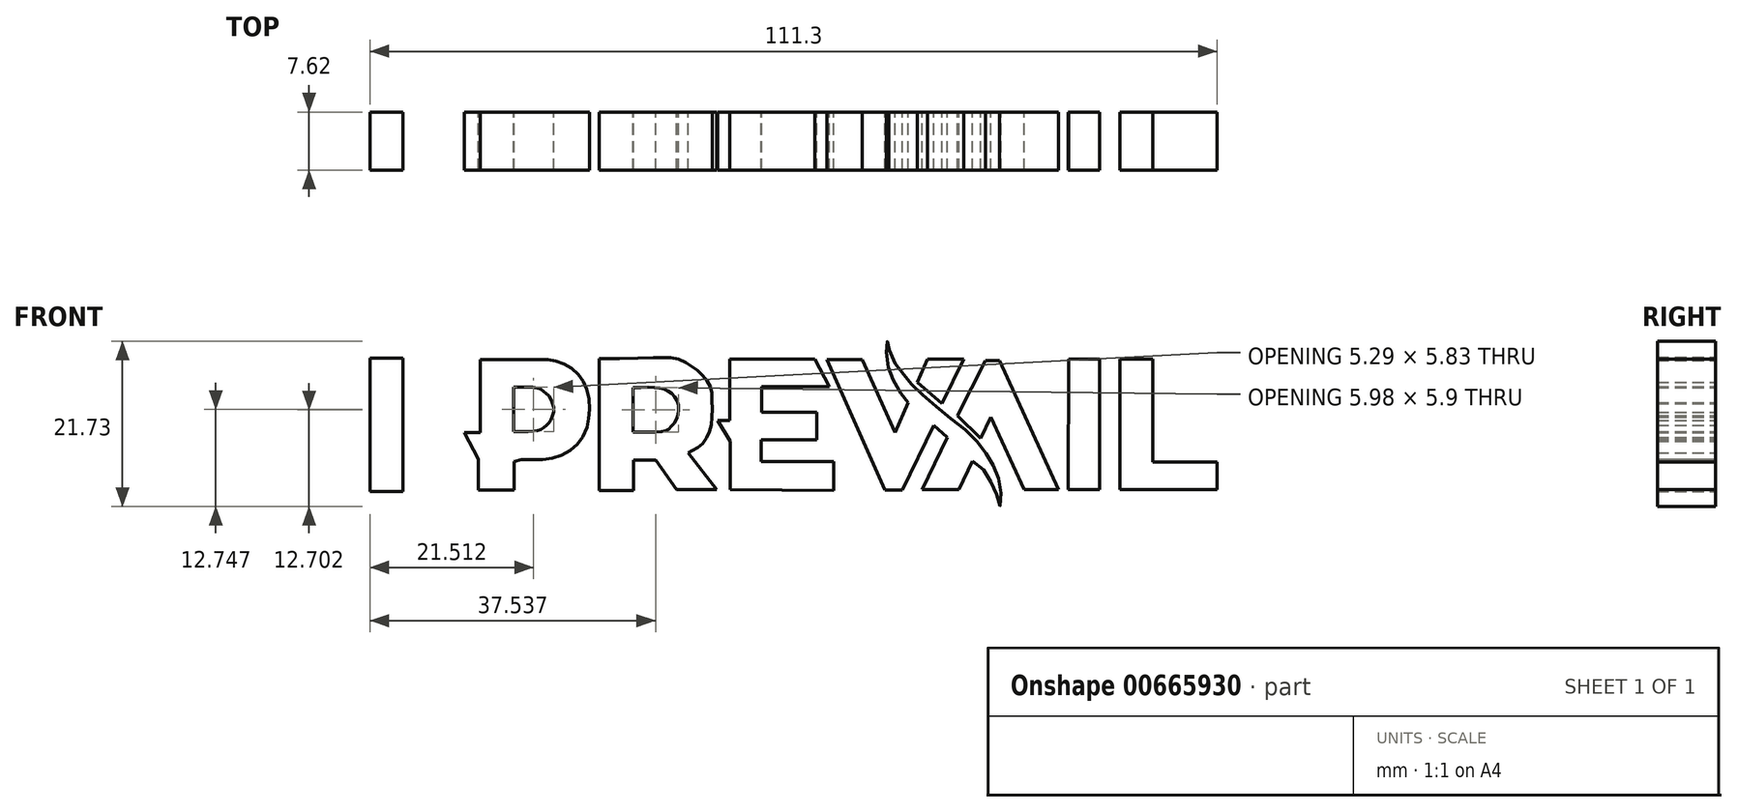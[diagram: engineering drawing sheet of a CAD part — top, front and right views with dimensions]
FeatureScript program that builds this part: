
annotation { "Feature Type Name" : "Feature", "Feature Type Description" : "" }
export const myFeature = defineFeature(function(context is Context, id is Id, definition is map)
    precondition{}
    {
        {
            var Q0;
            Q0=qCreatedBy(makeId("Front.planeOp"),FACE);
            var sketch = newSketch(context, id + "F0", { "sketchPlane" : qUnion([Q0])});
            skLineSegment(sketch, "E0", {"start": v(-55.42, 8.61) * mm, "end": v(-51.05, 8.61) * mm});
            skLineSegment(sketch, "E1", {"start": v(-51.05, 8.61) * mm, "end": v(-51.05, -8.88) * mm});
            skLineSegment(sketch, "E2", {"start": v(-51.05, -8.88) * mm, "end": v(-55.4, -8.88) * mm});
            skLineSegment(sketch, "E3", {"start": v(-55.4, -8.88) * mm, "end": v(-55.42, 8.61) * mm});
            skLineSegment(sketch, "E4", {"start": v(-43, -1.15) * mm, "end": v(-40.93, -1.15) * mm});
            skLineSegment(sketch, "E5", {"start": v(-40.93, -1.15) * mm, "end": v(-40.93, 8.45) * mm});
            skLineSegment(sketch, "E6", {"start": v(-43, -1.15) * mm, "end": v(-41.17, -4.64) * mm});
            skLineSegment(sketch, "E7", {"start": v(-41.17, -4.64) * mm, "end": v(-41.17, -8.71) * mm});
            skLineSegment(sketch, "E8", {"start": v(-41.17, -8.71) * mm, "end": v(-36.49, -8.71) * mm});
            skLineSegment(sketch, "E9", {"start": v(-36.49, -8.71) * mm, "end": v(-36.49, -4.95) * mm});
            skLineSegment(sketch, "E10", {"start": v(-36.55, 4.78) * mm, "end": v(-36.55, -1.05) * mm});
            skFitSpline(sketch, "E11", {"points": [v(-40.93, 8.45) * mm, v(-33.7, 8.45) * mm, v(-32.38, 8.45) * mm, v(-31.47, 8.34) * mm, v(-30.55, 8.07) * mm, v(-29.4, 7.62) * mm, v(-28.36, 6.8) * mm, v(-27.68, 6) * mm, v(-27.12, 5) * mm, v(-26.72, 3.78) * mm, v(-26.55, 2.03) * mm, v(-26.68, 0.64) * mm, v(-26.87, -0.46) * mm, v(-27.62, -2.02) * mm, v(-28.35, -2.86) * mm, v(-29.63, -3.85) * mm, v(-30.87, -4.4) * mm, v(-32.43, -4.68) * mm, v(-33.8, -4.69) * mm, v(-35.75, -4.72) * mm, v(-36.49, -4.95) * mm], "startDerivative": vector(78.04, -0.5) * mm, "endDerivative": vector(-6.77, -22.55) * mm});
            skFitSpline(sketch, "E12", {"points": [v(-36.55, 4.78) * mm, v(-34.11, 4.78) * mm, v(-33.12, 4.59) * mm, v(-32.49, 4.14) * mm, v(-31.95, 3.67) * mm, v(-31.5, 2.82) * mm, v(-31.26, 1.8) * mm, v(-31.59, 0.62) * mm, v(-31.99, 0) * mm, v(-32.59, -0.49) * mm, v(-33.17, -0.85) * mm, v(-33.87, -0.97) * mm, v(-36.55, -1.05) * mm], "startDerivative": vector(21.47, 0.42) * mm, "endDerivative": vector(-23.73, -0.4) * mm});
            skLineSegment(sketch, "E13", {"start": v(-25.3, -8.76) * mm, "end": v(-20.82, -8.76) * mm});
            skLineSegment(sketch, "E14", {"start": v(-20.82, -8.76) * mm, "end": v(-20.82, -4.8) * mm});
            skLineSegment(sketch, "E15", {"start": v(-20.82, -4.8) * mm, "end": v(-17.85, -4.8) * mm});
            skLineSegment(sketch, "E16", {"start": v(-17.85, -4.8) * mm, "end": v(-15.14, -8.67) * mm});
            skLineSegment(sketch, "E17", {"start": v(-15.14, -8.67) * mm, "end": v(-9.87, -8.67) * mm});
            skLineSegment(sketch, "E18", {"start": v(-9.87, -8.67) * mm, "end": v(-13.63, -3.85) * mm});
            skLineSegment(sketch, "E19", {"start": v(-25.3, -8.76) * mm, "end": v(-25.3, 8.55) * mm});
            skLineSegment(sketch, "E20", {"start": v(-20.87, -1.13) * mm, "end": v(-20.87, 4.72) * mm});
            skLineSegment(sketch, "E21", {"start": v(-8.12, -8.66) * mm, "end": v(-8.12, -2.32) * mm});
            skLineSegment(sketch, "E22", {"start": v(-8.12, -2.32) * mm, "end": v(-9.76, 0.46) * mm});
            skLineSegment(sketch, "E23", {"start": v(-9.76, 0.46) * mm, "end": v(-8.17, 0.46) * mm});
            skLineSegment(sketch, "E24", {"start": v(-8.17, 0.46) * mm, "end": v(-8.17, 8.5) * mm});
            skLineSegment(sketch, "E25", {"start": v(-8.17, 8.5) * mm, "end": v(3, 8.5) * mm});
            skLineSegment(sketch, "E26", {"start": v(3, 8.5) * mm, "end": v(4.94, 4.9) * mm});
            skLineSegment(sketch, "E27", {"start": v(4.94, 4.9) * mm, "end": v(-3.97, 4.9) * mm});
            skLineSegment(sketch, "E28", {"start": v(-3.97, 4.9) * mm, "end": v(-3.97, 1.5) * mm});
            skLineSegment(sketch, "E29", {"start": v(-3.97, 1.5) * mm, "end": v(3.3, 1.5) * mm});
            skLineSegment(sketch, "E30", {"start": v(3.3, 1.5) * mm, "end": v(3.3, -2.12) * mm});
            skLineSegment(sketch, "E31", {"start": v(3.3, -2.12) * mm, "end": v(-4, -2.12) * mm});
            skLineSegment(sketch, "E32", {"start": v(-4, -2.12) * mm, "end": v(-4, -4.98) * mm});
            skLineSegment(sketch, "E33", {"start": v(-4, -4.98) * mm, "end": v(5.47, -4.98) * mm});
            skLineSegment(sketch, "E34", {"start": v(5.47, -4.98) * mm, "end": v(5.47, -8.77) * mm});
            skLineSegment(sketch, "E35", {"start": v(5.47, -8.77) * mm, "end": v(-8.12, -8.66) * mm});
            skLineSegment(sketch, "E36", {"start": v(4.63, 8.45) * mm, "end": v(9.25, 8.45) * mm});
            skLineSegment(sketch, "E37", {"start": v(9.25, 8.45) * mm, "end": v(13.53, -1.19) * mm});
            skLineSegment(sketch, "E38", {"start": v(13.53, -1.19) * mm, "end": v(15.3, 2.75) * mm});
            skLineSegment(sketch, "E39", {"start": v(4.63, 8.45) * mm, "end": v(12.25, -8.72) * mm});
            skLineSegment(sketch, "E40", {"start": v(12.25, -8.72) * mm, "end": v(14.5, -8.72) * mm});
            skLineSegment(sketch, "E41", {"start": v(14.5, -8.72) * mm, "end": v(18.63, -0.22) * mm});
            skLineSegment(sketch, "E42", {"start": v(18.63, -0.22) * mm, "end": v(20.43, -1.81) * mm});
            skLineSegment(sketch, "E43", {"start": v(20.43, -1.81) * mm, "end": v(17.09, -8.68) * mm});
            skLineSegment(sketch, "E44", {"start": v(17.09, -8.68) * mm, "end": v(21.91, -8.68) * mm});
            skLineSegment(sketch, "E45", {"start": v(21.91, -8.68) * mm, "end": v(23.75, -4.91) * mm});
            skLineSegment(sketch, "E46", {"start": v(16.49, 5.48) * mm, "end": v(19.7, 2.63) * mm});
            skLineSegment(sketch, "E47", {"start": v(19.7, 2.63) * mm, "end": v(22.59, 8.47) * mm});
            skLineSegment(sketch, "E48", {"start": v(22.59, 8.47) * mm, "end": v(17.83, 8.47) * mm});
            skLineSegment(sketch, "E49", {"start": v(17.83, 8.47) * mm, "end": v(16.49, 5.48) * mm});
            skLineSegment(sketch, "E50", {"start": v(21.74, 1.1) * mm, "end": v(24.77, -1.93) * mm});
            skLineSegment(sketch, "E51", {"start": v(24.77, -1.93) * mm, "end": v(26.14, 0.85) * mm});
            skLineSegment(sketch, "E52", {"start": v(26.14, 0.85) * mm, "end": v(30.5, -8.63) * mm});
            skLineSegment(sketch, "E53", {"start": v(30.5, -8.63) * mm, "end": v(35.05, -8.63) * mm});
            skLineSegment(sketch, "E54", {"start": v(35.05, -8.63) * mm, "end": v(27.27, 8.3) * mm});
            skLineSegment(sketch, "E55", {"start": v(27.27, 8.3) * mm, "end": v(25.41, 8.3) * mm});
            skLineSegment(sketch, "E56", {"start": v(25.41, 8.3) * mm, "end": v(21.74, 1.1) * mm});
            skLineSegment(sketch, "E57", {"start": v(36.26, -8.63) * mm, "end": v(40.41, -8.63) * mm});
            skLineSegment(sketch, "E58", {"start": v(40.41, -8.63) * mm, "end": v(40.41, 8.47) * mm});
            skLineSegment(sketch, "E59", {"start": v(40.41, 8.47) * mm, "end": v(36.34, 8.47) * mm});
            skLineSegment(sketch, "E60", {"start": v(36.26, -8.63) * mm, "end": v(36.34, 8.47) * mm});
            skLineSegment(sketch, "E61", {"start": v(43.07, 8.47) * mm, "end": v(47.44, 8.47) * mm});
            skLineSegment(sketch, "E62", {"start": v(47.44, 8.47) * mm, "end": v(47.44, -5.04) * mm});
            skLineSegment(sketch, "E63", {"start": v(47.44, -5.04) * mm, "end": v(55.88, -5.04) * mm});
            skLineSegment(sketch, "E64", {"start": v(55.88, -5.04) * mm, "end": v(55.88, -8.63) * mm});
            skLineSegment(sketch, "E65", {"start": v(55.88, -8.63) * mm, "end": v(43.07, -8.63) * mm});
            skLineSegment(sketch, "E66", {"start": v(43.07, -8.63) * mm, "end": v(43.07, 8.47) * mm});
            skFitSpline(sketch, "E67", {"points": [v(23.75, -4.91) * mm, v(24.93, -5.78) * mm, v(25.54, -6.66) * mm, v(26.37, -8.05) * mm, v(26.92, -9.35) * mm, v(27.3, -10.88) * mm, v(27.4, -10.63) * mm, v(27.5, -9.38) * mm, v(27.29, -7.78) * mm, v(26.84, -6.39) * mm, v(26.31, -5.16) * mm, v(25.56, -3.95) * mm, v(24.56, -2.67) * mm, v(23.35, -1.34) * mm, v(21.63, 0.12) * mm, v(19.77, 1.62) * mm, v(17.81, 3.27) * mm, v(16.41, 4.47) * mm, v(15.41, 5.57) * mm, v(14.81, 6.34) * mm, v(13.95, 7.33) * mm, v(13.14, 8.69) * mm, v(12.72, 10.05) * mm, v(12.68, 10.83) * mm, v(12.5, 10.82) * mm, v(12.42, 10.32) * mm, v(12.4, 8.77) * mm, v(12.7, 7.27) * mm, v(13.15, 6.16) * mm, v(13.98, 4.46) * mm, v(14.71, 3.57) * mm, v(15.3, 2.75) * mm], "startDerivative": vector(39.33, -24.9) * mm, "endDerivative": vector(19.84, -30.43) * mm});
            skFitSpline(sketch, "E68", {"points": [v(-13.63, -3.85) * mm, v(-12.98, -3.5) * mm, v(-12.07, -2.95) * mm, v(-11.3, -2.04) * mm, v(-10.75, -0.8) * mm, v(-10.49, 0.66) * mm, v(-10.47, 2.63) * mm, v(-10.54, 4.23) * mm, v(-10.9, 5.29) * mm, v(-11.8, 6.43) * mm, v(-12.85, 7.34) * mm, v(-14.05, 8.12) * mm, v(-15.68, 8.67) * mm, v(-17.29, 8.68) * mm, v(-25.3, 8.55) * mm], "startDerivative": vector(13, 6.95) * mm, "endDerivative": vector(-61.43, -0.58) * mm});
            skFitSpline(sketch, "E69", {"points": [v(-20.87, 4.72) * mm, v(-17.6, 4.72) * mm, v(-16.3, 4.31) * mm, v(-15.3, 3.41) * mm, v(-14.87, 2.1) * mm, v(-15.2, 0.52) * mm, v(-15.99, -0.51) * mm, v(-16.63, -0.96) * mm, v(-18.87, -1.12) * mm, v(-20.87, -1.13) * mm], "startDerivative": vector(23.29, 0.96) * mm, "endDerivative": vector(-15.27, -0.07) * mm});
            skSolve(sketch);
        }
        {
            var Q0;
            Q0=makeQuery(id+"F0.imprint","IMPRINT",FACE,{"disambiguationData":[TD([[makeQuery(id+"F0.imprint","IMPRINT",EDGE,{"derivedFrom":sQuery(id+"F0.wireOp",EDGE,"E4")}),-1.0]])]});
            var Q1;
            Q1=makeQuery(id+"F0.imprint","IMPRINT",FACE,{"disambiguationData":[TD([[makeQuery(id+"F0.imprint","IMPRINT",EDGE,{"derivedFrom":sQuery(id+"F0.wireOp",EDGE,"E0")}),-1.0]])]});
            var Q2;
            Q2=makeQuery(id+"F0.imprint","IMPRINT",FACE,{"disambiguationData":[TD([[makeQuery(id+"F0.imprint","IMPRINT",EDGE,{"derivedFrom":sQuery(id+"F0.wireOp",EDGE,"E21")}),-1.0]])]});
            var Q3;
            Q3=makeQuery(id+"F0.imprint","IMPRINT",FACE,{"disambiguationData":[TD([[makeQuery(id+"F0.imprint","IMPRINT",EDGE,{"derivedFrom":sQuery(id+"F0.wireOp",EDGE,"E36")}),-1.0]])]});
            var Q4;
            Q4=makeQuery(id+"F0.imprint","IMPRINT",FACE,{"disambiguationData":[TD([[makeQuery(id+"F0.imprint","IMPRINT",EDGE,{"derivedFrom":sQuery(id+"F0.wireOp",EDGE,"E46")}),1.0]])]});
            var Q5;
            Q5=makeQuery(id+"F0.imprint","IMPRINT",FACE,{"disambiguationData":[TD([[makeQuery(id+"F0.imprint","IMPRINT",EDGE,{"derivedFrom":sQuery(id+"F0.wireOp",EDGE,"E50")}),1.0]])]});
            var Q6;
            Q6=makeQuery(id+"F0.imprint","IMPRINT",FACE,{"disambiguationData":[TD([[makeQuery(id+"F0.imprint","IMPRINT",EDGE,{"derivedFrom":sQuery(id+"F0.wireOp",EDGE,"E57")}),1.0]])]});
            var Q7;
            Q7=makeQuery(id+"F0.imprint","IMPRINT",FACE,{"disambiguationData":[TD([[makeQuery(id+"F0.imprint","IMPRINT",EDGE,{"derivedFrom":sQuery(id+"F0.wireOp",EDGE,"E61")}),-1.0]])]});
            var Q8;
            Q8=makeQuery(id+"F0.imprint","IMPRINT",FACE,{"disambiguationData":[TD([[makeQuery(id+"F0.imprint","IMPRINT",EDGE,{"derivedFrom":sQuery(id+"F0.wireOp",EDGE,"E13")}),1.0]])]});
            extrude(context, id + "F1", {"entities" : qUnion([Q0, Q1, Q2, Q3, Q4, Q5, Q6, Q7, Q8]), "depth" : 7.62 * mm, "offsetDistance" : 25.4 * mm});
        }
    });
